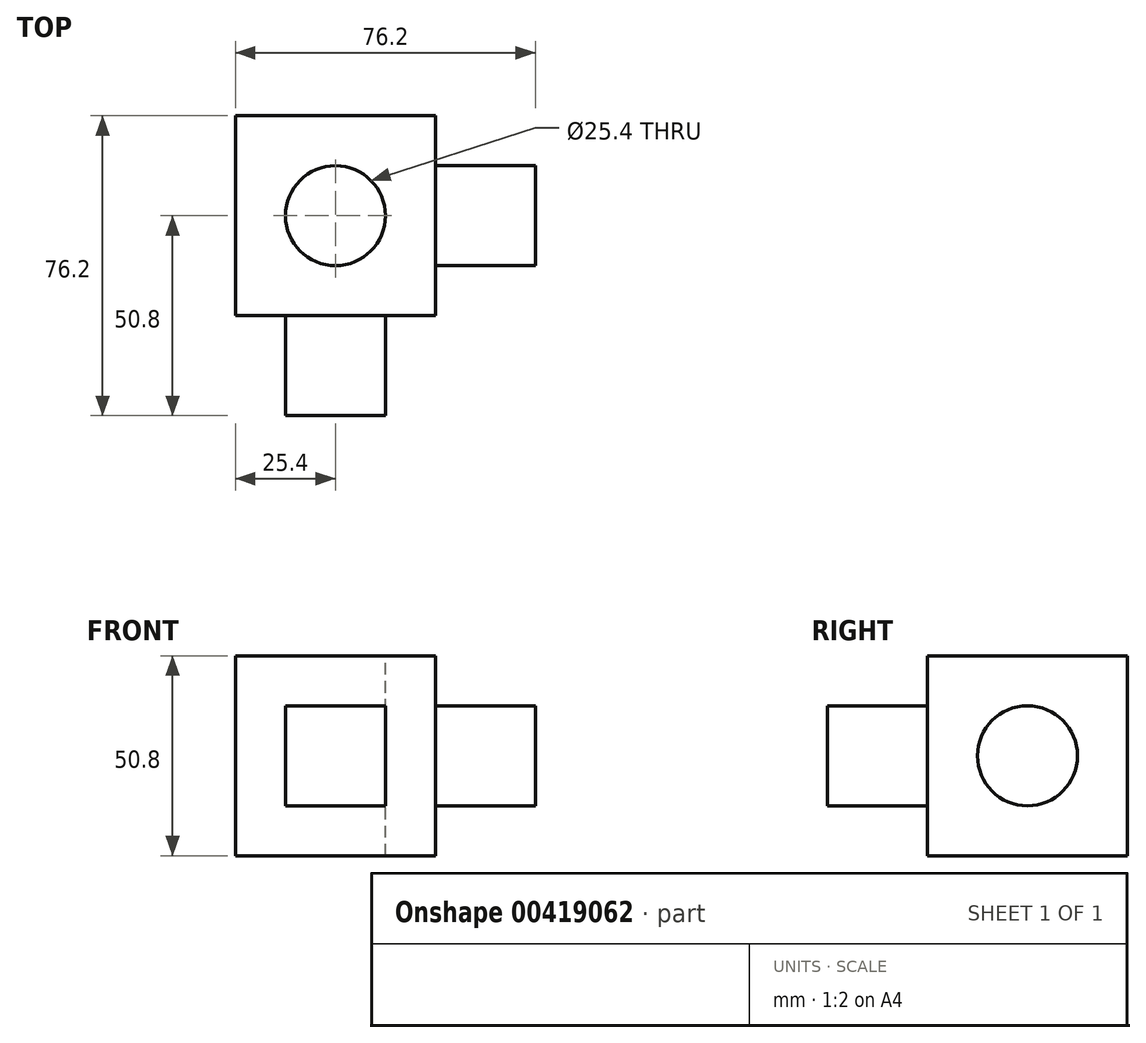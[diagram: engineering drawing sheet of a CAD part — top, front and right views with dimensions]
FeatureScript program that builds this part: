
annotation { "Feature Type Name" : "Feature", "Feature Type Description" : "" }
export const myFeature = defineFeature(function(context is Context, id is Id, definition is map)
    precondition{}
    {
        {
            var Q0;
            Q0=qCreatedBy(makeId("Front.planeOp"),FACE);
            var sketch = newSketch(context, id + "F0", { "sketchPlane" : qUnion([Q0])});
            skLineSegment(sketch, "E0", {"start": v(0, 0) * mm, "end": v(0, 50.8) * mm});
            skLineSegment(sketch, "E1", {"start": v(0, 0) * mm, "end": v(-50.8, 0) * mm});
            skLineSegment(sketch, "E2", {"start": v(-50.8, 0) * mm, "end": v(-50.8, 50.8) * mm});
            skLineSegment(sketch, "E3", {"start": v(-50.8, 50.8) * mm, "end": v(0, 50.8) * mm});
            skSolve(sketch);
        }
        {
            var Q0;
            Q0=makeQuery(id+"F0.imprint","IMPRINT",FACE,{"disambiguationData":[TD([[makeQuery(id+"F0.imprint","IMPRINT",EDGE,{"derivedFrom":sQuery(id+"F0.wireOp",EDGE,"E0")}),1.0]])]});
            extrude(context, id + "F1", {"entities" : qUnion([Q0]), "depth" : 50.8 * mm});
        }
        {
            var Q0;
            Q0=makeQuery(id+"F1.opExtrude","CAP_FACE",FACE,{"disambiguationData":[OSD([sQuery(id+"F0.wireOp",EDGE,"E0"),sQuery(id+"F0.wireOp",EDGE,"E1"),sQuery(id+"F0.wireOp",EDGE,"E2"),sQuery(id+"F0.wireOp",EDGE,"E3")])],"isStart":false});
            var sketch = newSketch(context, id + "F2", { "sketchPlane" : qUnion([Q0])});
            skLineSegment(sketch, "E4.bottom", {"start": v(-38.1, 12.7) * mm, "end": v(-12.7, 12.7) * mm});
            skLineSegment(sketch, "E4.top", {"start": v(-38.1, 38.1) * mm, "end": v(-12.7, 38.1) * mm});
            skLineSegment(sketch, "E4.left", {"start": v(-38.1, 12.7) * mm, "end": v(-38.1, 38.1) * mm});
            skLineSegment(sketch, "E4.right", {"start": v(-12.7, 12.7) * mm, "end": v(-12.7, 38.1) * mm});
            skSolve(sketch);
        }
        {
            var Q0;
            Q0=makeQuery(id+"F2.imprint","IMPRINT",FACE,{"disambiguationData":[TD([[makeQuery(id+"F2.imprint","IMPRINT",EDGE,{"derivedFrom":sQuery(id+"F2.wireOp",EDGE,"E4.bottom")}),1.0]])]});
            extrude(context, id + "F3", {"entities" : qUnion([Q0]), "operationType" : NewBodyOperationType.ADD, "depth" : 25.4 * mm});
        }
        {
            var Q0;
            Q0=makeQuery(id+"F1.opExtrude","SWEPT_FACE",FACE,{"disambiguationData":[OSD([sQuery(id+"F0.wireOp",EDGE,"E0")])]});
            var sketch = newSketch(context, id + "F4", { "sketchPlane" : qUnion([Q0])});
            skCircle(sketch, "E5", {"center": v(-25.4, 25.4) * mm, "radius": 12.7 * mm});
            skSolve(sketch);
        }
        {
            var Q0;
            Q0=makeQuery(id+"F4.imprint","IMPRINT",FACE,{"disambiguationData":[TD([[makeQuery(id+"F4.imprint","IMPRINT",EDGE,{"derivedFrom":sQuery(id+"F4.wireOp",EDGE,"E5")}),1.0]])]});
            extrude(context, id + "F5", {"entities" : qUnion([Q0]), "operationType" : NewBodyOperationType.ADD, "depth" : 25.4 * mm});
        }
        {
            var Q0;
            Q0=makeQuery(id+"F1.opExtrude","SWEPT_FACE",FACE,{"disambiguationData":[OSD([sQuery(id+"F0.wireOp",EDGE,"E3")])]});
            var sketch = newSketch(context, id + "F6", { "sketchPlane" : qUnion([Q0])});
            skCircle(sketch, "E6", {"center": v(-25.4, -25.4) * mm, "radius": 12.7 * mm});
            skSolve(sketch);
        }
        {
            var Q0;
            Q0=makeQuery(id+"F6.imprint","IMPRINT",FACE,{"disambiguationData":[TD([[makeQuery(id+"F6.imprint","IMPRINT",EDGE,{"derivedFrom":sQuery(id+"F6.wireOp",EDGE,"E6")}),1.0]])]});
            extrude(context, id + "F7", {"entities" : qUnion([Q0]), "operationType" : NewBodyOperationType.REMOVE, "oppositeDirection" : true, "depth" : 50.8 * mm});
        }
    });
